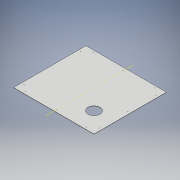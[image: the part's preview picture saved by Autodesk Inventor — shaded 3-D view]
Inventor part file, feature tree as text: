
AUTODESK INVENTOR PART (.ipt)
format: ipt  version: 2018 (Build 220112000, 112)  size: 130,048 bytes
history: native  units: mm
features: other x1, extrude x1, sketch x1
ambient origin geometry x8: Origin, YZ Plane, XZ Plane, XY Plane, X Axis, Y Axis, Z Axis, Center Point
bodies: Body1 (feature_tree)
feature tree (3):
  other  "Bryła1"
  extrude  "Wyciągnięcie proste1"  Depth=1000.0mm
  sketch  "Szkic1"
